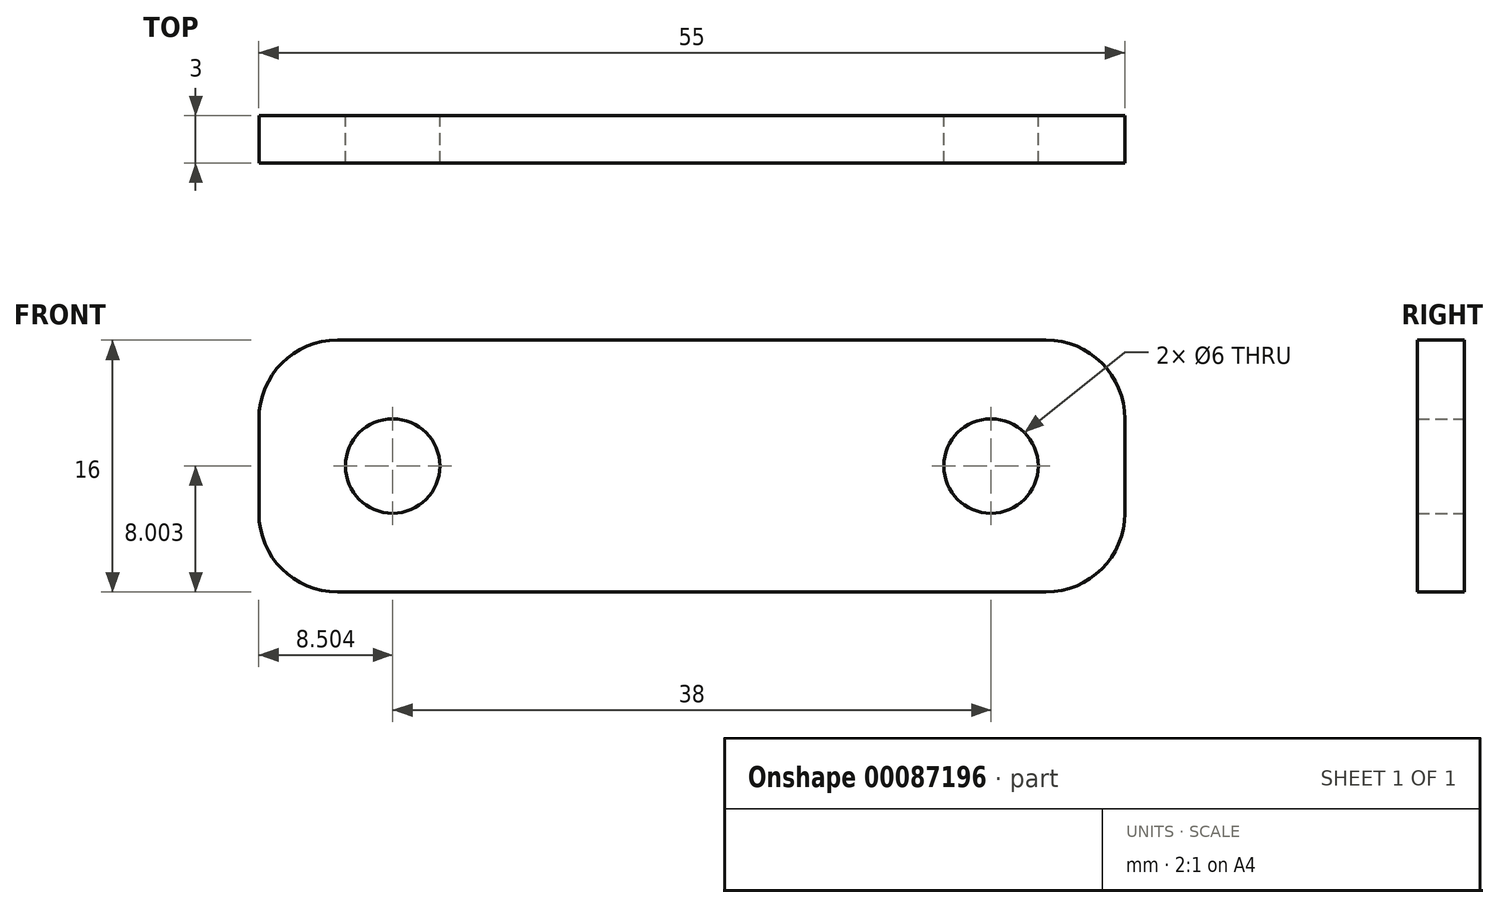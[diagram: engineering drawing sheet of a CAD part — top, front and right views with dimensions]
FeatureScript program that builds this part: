
annotation { "Feature Type Name" : "Feature", "Feature Type Description" : "" }
export const myFeature = defineFeature(function(context is Context, id is Id, definition is map)
    precondition{}
    {
        {
            var Q0;
            Q0=qCreatedBy(makeId("Front.planeOp"),FACE);
            var sketch = newSketch(context, id + "F0", { "sketchPlane" : qUnion([Q0])});
            skLineSegment(sketch, "E0", {"start": v(-166.94, 33.38) * mm, "end": v(-128.94, 33.38) * mm, "construction": true});
            skCircle(sketch, "E1", {"center": v(-166.94, 33.38) * mm, "radius": 3 * mm});
            skCircle(sketch, "E2", {"center": v(-128.94, 33.38) * mm, "radius": 3 * mm});
            skLineSegment(sketch, "E3.bottom", {"start": v(-125.44, 41.38) * mm, "end": v(-170.44, 41.38) * mm});
            skLineSegment(sketch, "E3.top", {"start": v(-125.44, 25.38) * mm, "end": v(-170.44, 25.38) * mm});
            skLineSegment(sketch, "E3.left", {"start": v(-120.44, 36.38) * mm, "end": v(-120.44, 30.38) * mm});
            skLineSegment(sketch, "E3.right", {"start": v(-175.44, 36.38) * mm, "end": v(-175.44, 30.38) * mm});
            skPoint(sketch, "E3.middle", {"position": v(-147.94, 33.38) * mm});
            skPoint(sketch, "E4.visualSharp", {"position": v(-120.44, 41.38) * mm});
            skArc(sketch, "E4.filletArc", {"start": v(-120.44, 36.38) * mm, "mid": v(-121.9, 39.92) * mm, "end": v(-125.44, 41.38) * mm});
            skPoint(sketch, "E5.visualSharp", {"position": v(-120.44, 25.38) * mm});
            skArc(sketch, "E5.filletArc", {"start": v(-125.44, 25.38) * mm, "mid": v(-121.9, 26.85) * mm, "end": v(-120.44, 30.38) * mm});
            skPoint(sketch, "E6.visualSharp", {"position": v(-175.44, 25.38) * mm});
            skArc(sketch, "E6.filletArc", {"start": v(-175.44, 30.38) * mm, "mid": v(-173.97, 26.85) * mm, "end": v(-170.44, 25.38) * mm});
            skPoint(sketch, "E7.visualSharp", {"position": v(-175.44, 41.38) * mm});
            skArc(sketch, "E7.filletArc", {"start": v(-170.44, 41.38) * mm, "mid": v(-173.97, 39.92) * mm, "end": v(-175.44, 36.38) * mm});
            skSolve(sketch);
        }
        {
            var Q0;
            Q0=qSketchRegion(id+"F0",true);
            extrude(context, id + "F1", {"entities" : qUnion([Q0]), "depth" : 3 * mm});
        }
    });
